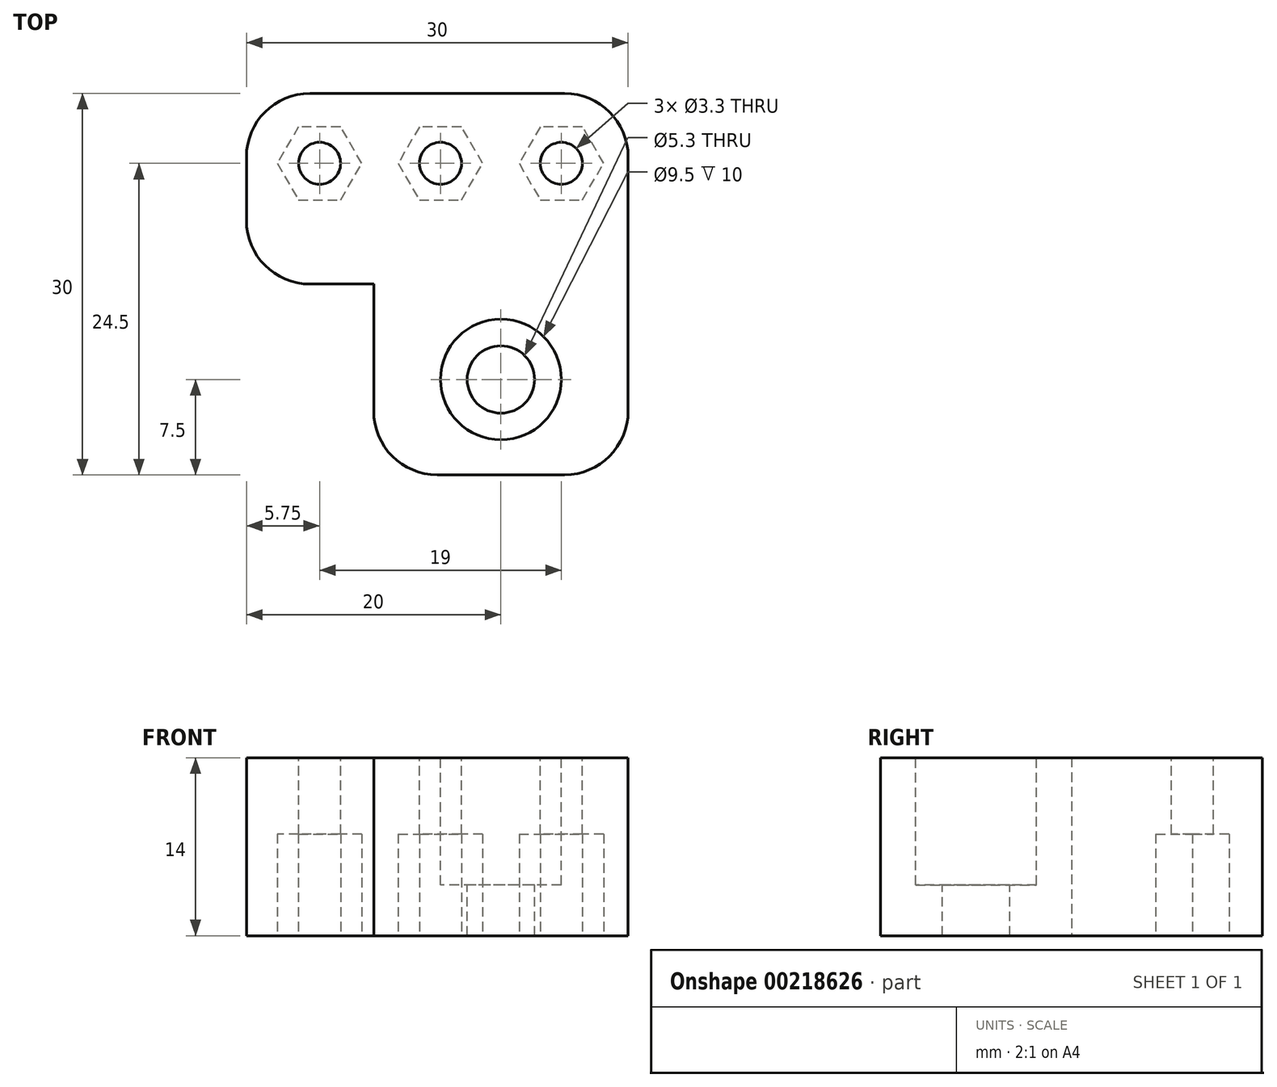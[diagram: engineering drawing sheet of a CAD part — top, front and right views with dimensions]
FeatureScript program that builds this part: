
annotation { "Feature Type Name" : "Feature", "Feature Type Description" : "" }
export const myFeature = defineFeature(function(context is Context, id is Id, definition is map)
    precondition{}
    {
        {
            var Q0;
            Q0=qCreatedBy(makeId("Top.planeOp"),FACE);
            var sketch = newSketch(context, id + "F0", { "sketchPlane" : qUnion([Q0])});
            skLineSegment(sketch, "E0.bottom", {"start": v(10, -15) * mm, "end": v(-10, -15) * mm});
            skLineSegment(sketch, "E0.top", {"start": v(10, 15) * mm, "end": v(-10, 15) * mm});
            skLineSegment(sketch, "E0.left", {"start": v(10, -15) * mm, "end": v(10, 15) * mm});
            skLineSegment(sketch, "E0.right", {"start": v(-10, -15) * mm, "end": v(-10, 15) * mm});
            skPoint(sketch, "E0.middle", {"position": v(0, 0) * mm});
            skSolve(sketch);
        }
        {
            var Q0;
            Q0 = qSketchRegion(id + "F0", true);
            extrude(context, id + "F1", {"entities" : qUnion([Q0]), "depth" : 14 * mm, "offsetDistance" : 25 * mm});
        }
        {
            var Q0;
            Q0=makeQuery(id+"F1.opExtrude","CAP_FACE",FACE,{"disambiguationData":[OSD([sQuery(id+"F0.wireOp",EDGE,"E0.bottom"),sQuery(id+"F0.wireOp",EDGE,"E0.top"),sQuery(id+"F0.wireOp",EDGE,"E0.left"),sQuery(id+"F0.wireOp",EDGE,"E0.right")])],"isStart":false});
            var sketch = newSketch(context, id + "F2", { "sketchPlane" : qUnion([Q0])});
            skCircle(sketch, "E1", {"center": v(0, -7.5) * mm, "radius": 2.65 * mm});
            skSolve(sketch);
        }
        {
            var Q0;
            Q0 = qSketchRegion(id + "F2", true);
            extrude(context, id + "F3", {"entities" : qUnion([Q0]), "operationType" : NewBodyOperationType.REMOVE, "endBound" : BoundingType.THROUGH_ALL, "oppositeDirection" : true, "depth" : 25 * mm});
        }
        {
            var Q0;
            Q0=makeQuery(id+"F1.opExtrude","CAP_FACE",FACE,{"disambiguationData":[OSD([sQuery(id+"F0.wireOp",EDGE,"E0.bottom"),sQuery(id+"F0.wireOp",EDGE,"E0.top"),sQuery(id+"F0.wireOp",EDGE,"E0.left"),sQuery(id+"F0.wireOp",EDGE,"E0.right")])],"isStart":false});
            var sketch = newSketch(context, id + "F4", { "sketchPlane" : qUnion([Q0])});
            skCircle(sketch, "E2", {"center": v(-4.75, 9.5) * mm, "radius": 1.65 * mm});
            skLineSegment(sketch, "E3", {"start": v(0, 0) * mm, "end": v(0, 22.08) * mm, "construction": true});
            skCircle(sketch, "E4", {"center": v(4.75, 9.5) * mm, "radius": 1.65 * mm});
            skSolve(sketch);
        }
        {
            var Q0;
            Q0 = qSketchRegion(id + "F4", true);
            extrude(context, id + "F5", {"entities" : qUnion([Q0]), "operationType" : NewBodyOperationType.REMOVE, "endBound" : BoundingType.THROUGH_ALL, "oppositeDirection" : true, "depth" : 25 * mm});
        }
        {
            var Q0;
            Q0=makeQuery(id+"F1.opExtrude","SWEPT_FACE",FACE,{"disambiguationData":[OSD([sQuery(id+"F0.wireOp",EDGE,"E0.right")])]});
            var sketch = newSketch(context, id + "F6", { "sketchPlane" : qUnion([Q0])});
            skPoint(sketch, "E5.oppositeSnap0", {"position": v(0, 0) * mm});
            skLineSegment(sketch, "E5.bottom", {"start": v(0, 14) * mm, "end": v(-15, 14) * mm});
            skLineSegment(sketch, "E5.top", {"start": v(0, 0) * mm, "end": v(-15, 0) * mm});
            skLineSegment(sketch, "E5.left", {"start": v(-15, 14) * mm, "end": v(-15, 0) * mm});
            skLineSegment(sketch, "E5.right", {"start": v(0, 14) * mm, "end": v(0, 0) * mm});
            skSolve(sketch);
        }
        {
            var Q0;
            Q0 = qSketchRegion(id + "F6", true);
            extrude(context, id + "F7", {"entities" : qUnion([Q0]), "operationType" : NewBodyOperationType.ADD, "depth" : 10 * mm});
        }
        {
            var Q0;
            Q0=makeQuery(id+"F7.boolean.opBoolean","MERGE",FACE,{"derivedFrom":[makeQuery(id+"F1.opExtrude","CAP_FACE",FACE,{"disambiguationData":[OSD([sQuery(id+"F0.wireOp",EDGE,"E0.bottom"),sQuery(id+"F0.wireOp",EDGE,"E0.top"),sQuery(id+"F0.wireOp",EDGE,"E0.left"),sQuery(id+"F0.wireOp",EDGE,"E0.right")])],"isStart":false}),makeQuery(id+"F7.opExtrude","SWEPT_FACE",FACE,{"disambiguationData":[OSD([sQuery(id+"F6.wireOp",EDGE,"E5.bottom")])]})]});
            var sketch = newSketch(context, id + "F8", { "sketchPlane" : qUnion([Q0])});
            skCircle(sketch, "E6", {"center": v(-14.25, 9.5) * mm, "radius": 1.65 * mm});
            skLineSegment(sketch, "E7", {"start": v(-14.25, 9.5) * mm, "end": v(-4.75, 9.5) * mm, "construction": true});
            skSolve(sketch);
        }
        {
            var Q0;
            Q0 = qSketchRegion(id + "F8", true);
            var Q1;
            Q1=sQuery(id+"F8.wireOp",EDGE,"JwcSaSVH-wO2g-acyu-GsNU-yalXvGiGOJmd");
            extrude(context, id + "F9", {"entities" : qUnion([Q0]), "operationType" : NewBodyOperationType.REMOVE, "surfaceEntities" : qUnion([Q1]), "endBound" : BoundingType.THROUGH_ALL, "oppositeDirection" : true, "depth" : 25 * mm});
        }
        {
            var Q0;
            Q0=makeQuery(id+"F1.opExtrude","SWEPT_EDGE",EDGE,{"disambiguationData":[OSD([sQuery(id+"F0.wireOp",EDGE,"E0.top"),sQuery(id+"F0.wireOp",EDGE,"E0.right")])]});
            var Q1;
            Q1=makeQuery(id+"F1.opExtrude","SWEPT_EDGE",EDGE,{"disambiguationData":[OSD([sQuery(id+"F0.wireOp",EDGE,"E0.bottom"),sQuery(id+"F0.wireOp",EDGE,"E0.right")])]});
            var Q2;
            Q2=makeQuery(id+"F1.opExtrude","SWEPT_EDGE",EDGE,{"disambiguationData":[OSD([sQuery(id+"F0.wireOp",EDGE,"E0.bottom"),sQuery(id+"F0.wireOp",EDGE,"E0.left")])]});
            var Q3;
            Q3=makeQuery(id+"F7.opExtrude","CAP_EDGE",EDGE,{"disambiguationData":[OSD([sQuery(id+"F6.wireOp",EDGE,"E5.right")])],"isStart":true});
            var Q4;
            Q4=makeQuery(id+"F7.opExtrude","CAP_EDGE",EDGE,{"disambiguationData":[OSD([sQuery(id+"F6.wireOp",EDGE,"E5.right")])],"isStart":false});
            var Q5;
            Q5=makeQuery(id+"F7.opExtrude","CAP_EDGE",EDGE,{"disambiguationData":[OSD([sQuery(id+"F6.wireOp",EDGE,"E5.left")])],"isStart":false});
            var Q6;
            Q6=makeQuery(id+"F1.opExtrude","SWEPT_EDGE",EDGE,{"disambiguationData":[OSD([sQuery(id+"F0.wireOp",EDGE,"E0.top"),sQuery(id+"F0.wireOp",EDGE,"E0.left")])]});
            fillet(context, id + "F10", {"entities" : qUnion([Q0, Q1, Q2, Q3, Q4, Q5, Q6]), "radius" : 5 * mm, "tangentPropagation" : true, "allowEdgeOverflow" : false});
        }
        {
            var Q0;
            Q0=makeQuery(id+"F7.boolean.opBoolean","MERGE",FACE,{"derivedFrom":[makeQuery(id+"F1.opExtrude","CAP_FACE",FACE,{"disambiguationData":[OSD([sQuery(id+"F0.wireOp",EDGE,"E0.bottom"),sQuery(id+"F0.wireOp",EDGE,"E0.top"),sQuery(id+"F0.wireOp",EDGE,"E0.left"),sQuery(id+"F0.wireOp",EDGE,"E0.right")])],"isStart":true}),makeQuery(id+"F7.opExtrude","SWEPT_FACE",FACE,{"disambiguationData":[OSD([sQuery(id+"F6.wireOp",EDGE,"E5.top")])]})]});
            var sketch = newSketch(context, id + "F11", { "sketchPlane" : qUnion([Q0])});
            skCircle(sketch, "E8.cCircle", {"center": v(-14.25, -9.5) * mm, "radius": 2.88 * mm, "construction": true});
            skLineSegment(sketch, "E8.0", {"start": v(-15.9, -12.38) * mm, "end": v(-17.57, -9.5) * mm});
            skLineSegment(sketch, "E8.1", {"start": v(-17.57, -9.5) * mm, "end": v(-15.9, -6.62) * mm});
            skLineSegment(sketch, "E8.2", {"start": v(-15.9, -6.62) * mm, "end": v(-12.6, -6.62) * mm});
            skLineSegment(sketch, "E8.3", {"start": v(-12.6, -6.63) * mm, "end": v(-10.93, -9.5) * mm});
            skLineSegment(sketch, "E8.4", {"start": v(-10.93, -9.5) * mm, "end": v(-12.6, -12.38) * mm});
            skLineSegment(sketch, "E8.5", {"start": v(-12.6, -12.38) * mm, "end": v(-15.9, -12.38) * mm});
            skPoint(sketch, "E8.0.midPoint", {"position": v(-16.74, -10.94) * mm});
            skCircle(sketch, "E9.cCircle", {"center": v(4.75, -9.5) * mm, "radius": 2.88 * mm, "construction": true});
            skLineSegment(sketch, "E9.0", {"start": v(1.43, -9.5) * mm, "end": v(3.1, -6.62) * mm});
            skLineSegment(sketch, "E9.1", {"start": v(3.1, -6.62) * mm, "end": v(6.4, -6.62) * mm});
            skLineSegment(sketch, "E9.2", {"start": v(6.4, -6.62) * mm, "end": v(8.07, -9.5) * mm});
            skLineSegment(sketch, "E9.3", {"start": v(8.07, -9.5) * mm, "end": v(6.4, -12.38) * mm});
            skLineSegment(sketch, "E9.4", {"start": v(6.4, -12.38) * mm, "end": v(3.1, -12.38) * mm});
            skLineSegment(sketch, "E9.5", {"start": v(3.1, -12.38) * mm, "end": v(1.43, -9.5) * mm});
            skPoint(sketch, "E9.0.midPoint", {"position": v(2.26, -8.06) * mm});
            skCircle(sketch, "E10.cCircle", {"center": v(-4.75, -9.5) * mm, "radius": 2.88 * mm, "construction": true});
            skLineSegment(sketch, "E10.0", {"start": v(-8.07, -9.5) * mm, "end": v(-6.4, -6.62) * mm});
            skLineSegment(sketch, "E10.1", {"start": v(-6.4, -6.63) * mm, "end": v(-3.1, -6.63) * mm});
            skLineSegment(sketch, "E10.2", {"start": v(-3.1, -6.63) * mm, "end": v(-1.43, -9.5) * mm});
            skLineSegment(sketch, "E10.3", {"start": v(-1.43, -9.5) * mm, "end": v(-3.1, -12.38) * mm});
            skLineSegment(sketch, "E10.4", {"start": v(-3.1, -12.38) * mm, "end": v(-6.4, -12.38) * mm});
            skLineSegment(sketch, "E10.5", {"start": v(-6.4, -12.37) * mm, "end": v(-8.07, -9.5) * mm});
            skPoint(sketch, "E10.0.midPoint", {"position": v(-7.24, -8.06) * mm});
            skSolve(sketch);
        }
        {
            var Q0;
            Q0 = qSketchRegion(id + "F11", true);
            extrude(context, id + "F12", {"entities" : qUnion([Q0]), "operationType" : NewBodyOperationType.REMOVE, "oppositeDirection" : true, "depth" : 8 * mm, "offsetDistance" : 25 * mm});
        }
        {
            var Q0;
            Q0=makeQuery(id+"F7.boolean.opBoolean","MERGE",FACE,{"derivedFrom":[makeQuery(id+"F1.opExtrude","CAP_FACE",FACE,{"disambiguationData":[OSD([sQuery(id+"F0.wireOp",EDGE,"E0.bottom"),sQuery(id+"F0.wireOp",EDGE,"E0.top"),sQuery(id+"F0.wireOp",EDGE,"E0.left"),sQuery(id+"F0.wireOp",EDGE,"E0.right")])],"isStart":false}),makeQuery(id+"F7.opExtrude","SWEPT_FACE",FACE,{"disambiguationData":[OSD([sQuery(id+"F6.wireOp",EDGE,"E5.bottom")])]})]});
            var sketch = newSketch(context, id + "F13", { "sketchPlane" : qUnion([Q0])});
            skCircle(sketch, "E11", {"center": v(0, -7.5) * mm, "radius": 4.75 * mm});
            skSolve(sketch);
        }
        {
            var Q0;
            Q0 = qSketchRegion(id + "F13", true);
            extrude(context, id + "F14", {"entities" : qUnion([Q0]), "operationType" : NewBodyOperationType.REMOVE, "oppositeDirection" : true, "depth" : 10 * mm, "offsetDistance" : 25 * mm});
        }
    });
